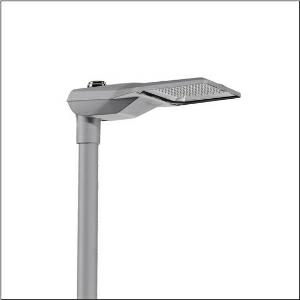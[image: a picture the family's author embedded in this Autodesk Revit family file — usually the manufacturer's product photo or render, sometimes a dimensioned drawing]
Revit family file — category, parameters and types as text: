
# Revit family: streetlight_sl_21_midi___p0_8a_5xe7u67n08mb_9091
name_source: partatom
category: Lighting Fixtures
units: mm (PartAtom-declared; Revit-internal decimal feet)

## family parameters
Cut with Voids When Loaded = No
Host = Face
Light Source = No
Part Type = Normal
Room Calculation Point = No
Round Connector Dimension = Use Diameter
Shared = No

## types (1)
- --- (1 x LED, 16380 lm, 134.3 W, 2700K)
    Apparent Load = 134 VA
    CIE Flux Codes = 33 69 96 100 100
    Color Rendering = 70
    Color Temperature = 2700K
    Default Elevation = 1800 mm
    Description = Streetlight SL 21 midi, mast luminaire, primary light control with lens, of PMMA, primary optical cover: cover, of toughened safety glass, transparent, light distribution: P0.8a, light emission: direct distribution, primary light characteristic: asymmetric, installation type: side-entry, LED, 3G 2.5mm², High Power LED, rated luminous flux: 16.380lm, luminous efficacy: 122lm/W, light colour: 727, colour temperature: 2700K, control gear: NEMA (7pin), control: flexible luminous flux parameterisation, time-dependent luminous flux control, constant luminous flux control, pre-setting: linear dimming characteristic, overheat protection, mains connection: 220..240V, AC, 50/60Hz, connection cable pre-assembled, cable length: 12,5m, wiring characteristics: H05VV-F, start of lifetime: 134W, end of service life: 141W, reduction: 60W, luminaire housing, of diecast aluminium (EN AC-44300), powder-coated, Siteco® metallic grey (DB 702S), corrosivity category C5 mid according to DIN EN ISO 12944, multi-level sealing system, sealing non-destructively replaceable, inclination adjustable: 0°, 5°, 10°, 15°, length: 644mm, width: 335mm, height: 110mm, spigot size: 42mm (side-entry), mounting height: 4..8m, protection rating (complete): IP66, insulation class (complete): insulation class I (protective earthing), certification: CE, ENEC, ENEC+, VDE, impact resistance: IK10, permissible operating ambient temperature for outdoor applications: -40..+50°C, standard-compliant lighting for roads and squares, packaging unit: 1 piece

Light Distribution: P0.8a
    Height = 111 mm
    Lamp = 1 x LED
    Lamp Light Flux = 16380 lm
    Lamp Power = 134.3 W
    Lamp count = 1
    Length = 644 mm
    Luminous efficacy = 122 lm/W
    Manufacturer = Siteco
    ModVariant = No
    Model = 5XE7U67N08MB
    Number of Poles = 1
    OnlyDefault = Yes
    Power Factor = 1
    Product Name = Streetlight SL 21 midi | P0.8a
    Product group = mast luminaire | pylon top
    ProductGroupID = 6100
    Protection Class = Protection class I
    Protection Degree = IP 66
    RLX_Detail_Level = 1
    RLX_Emergency_Light_Flux = 0 lm
    RLX_Emergency_Type = 0
    RLX_Emergency_Type_DB = No
    RlxData = <blob elided: 26233 chars, md5=ac133386>
    Socket = socket
    Standby Power = 0 W
    System Light Flux = 16381 lm
    System Power = 134 W
    Type Comments = factory setting: luminous flux: 100 % | dim-lin: 254 | 687 mA
    Type Image = l_1294377.jpg
    URL = http://relux.com
    VarID = @adj_073152
    Voltage = 0 V
    Weight = 0.00 kg
    Width = 336 mm

## geometry (parser evidence)
native form markers: Blend x4, Sweep x12
no freeform markers — native parametric forms only
